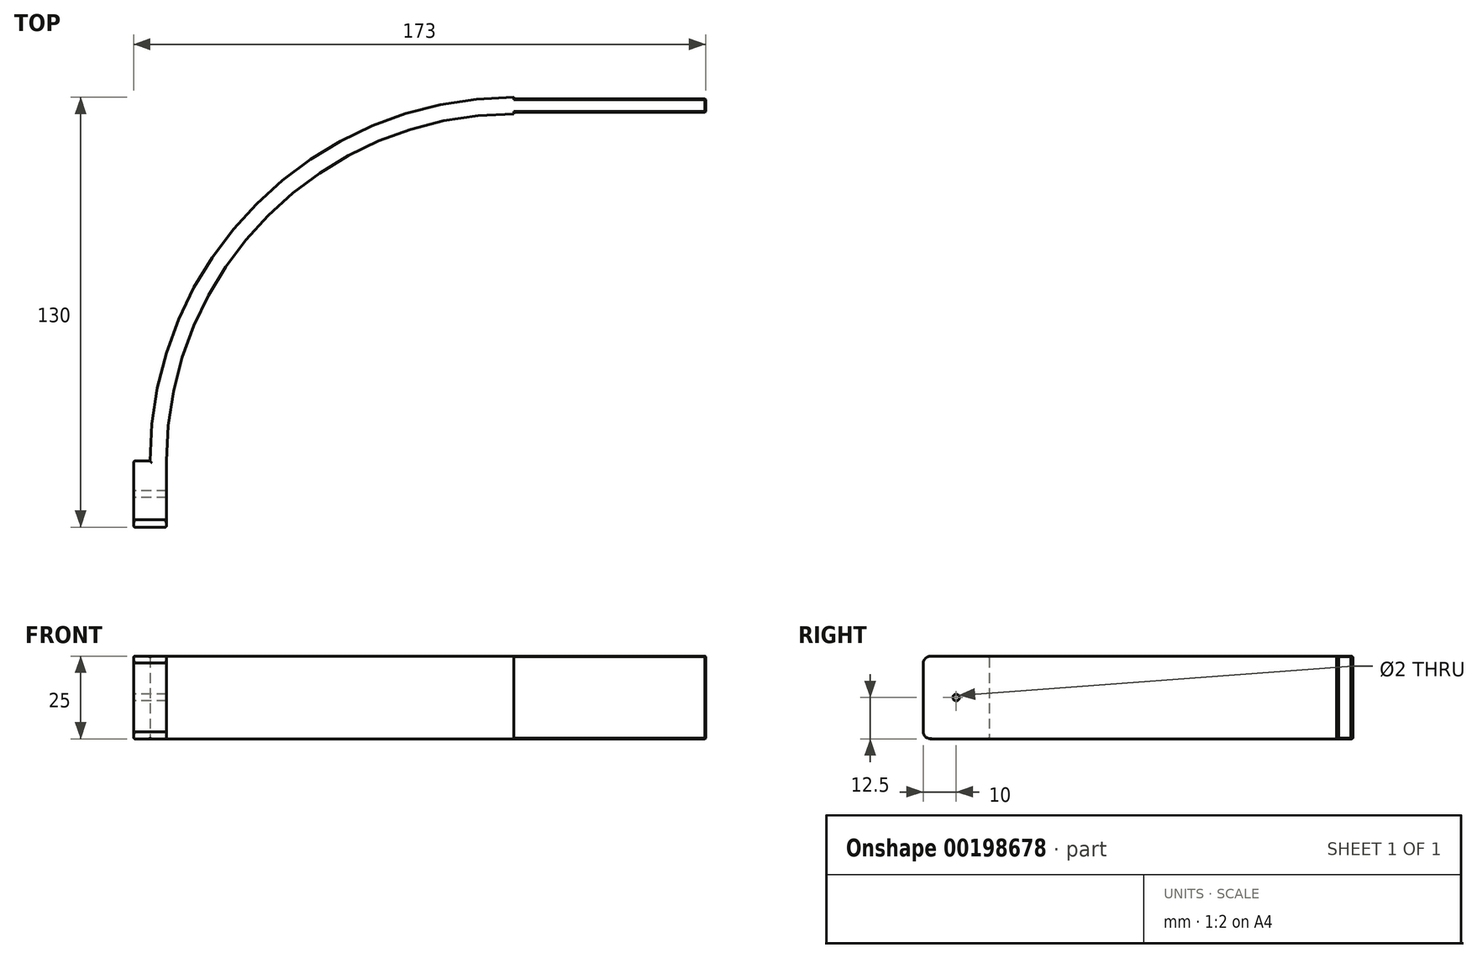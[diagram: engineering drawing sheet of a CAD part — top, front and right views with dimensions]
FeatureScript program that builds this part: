
annotation { "Feature Type Name" : "Feature", "Feature Type Description" : "" }
export const myFeature = defineFeature(function(context is Context, id is Id, definition is map)
    precondition{}
    {
        {
            var Q0;
            Q0=qCreatedBy(makeId("Top.planeOp"),FACE);
            var sketch = newSketch(context, id + "F0", { "sketchPlane" : qUnion([Q0])});
            skArc(sketch, "E0", {"start": v(-110, 0) * mm, "mid": v(-77.78, 77.78) * mm, "end": v(0, 110) * mm});
            skArc(sketch, "E1", {"start": v(-105, 0) * mm, "mid": v(-74.25, 74.25) * mm, "end": v(0, 105) * mm});
            skLineSegment(sketch, "E2", {"start": v(-105, -20) * mm, "end": v(-105, 0) * mm});
            skLineSegment(sketch, "E3", {"start": v(-110, 0) * mm, "end": v(-115, 0) * mm});
            skLineSegment(sketch, "E4", {"start": v(-115, 0) * mm, "end": v(-115, -20) * mm});
            skLineSegment(sketch, "E5", {"start": v(-115, -20) * mm, "end": v(-105, -20) * mm});
            skLineSegment(sketch, "E6", {"start": v(0, 110) * mm, "end": v(0, 109.5) * mm});
            skLineSegment(sketch, "E7", {"start": v(0, 109.5) * mm, "end": v(58, 109.5) * mm});
            skLineSegment(sketch, "E8", {"start": v(0, 105) * mm, "end": v(0, 105.5) * mm});
            skLineSegment(sketch, "E9", {"start": v(0, 105.5) * mm, "end": v(58, 105.5) * mm});
            skLineSegment(sketch, "E10", {"start": v(58, 105.5) * mm, "end": v(58, 109.5) * mm});
            skSolve(sketch);
        }
        {
            var Q0;
            Q0 = qSketchRegion(id + "F0", true);
            extrude(context, id + "F1", {"entities" : qUnion([Q0]), "depth" : 25 * mm});
        }
        {
            var Q0;
            Q0=makeQuery(id+"F1.opExtrude","SWEPT_FACE",FACE,{"disambiguationData":[OSD([sQuery(id+"F0.wireOp",EDGE,"E4")])]});
            var sketch = newSketch(context, id + "F2", { "sketchPlane" : qUnion([Q0])});
            skArc(sketch, "E11", {"start": v(17.52, 0) * mm, "mid": v(19.17, 0.55) * mm, "end": v(20, 2.09) * mm});
            skLineSegment(sketch, "E12", {"start": v(17.52, 0) * mm, "end": v(20, 0) * mm});
            skLineSegment(sketch, "E13", {"start": v(20, 0) * mm, "end": v(20, 2.09) * mm});
            skLineSegment(sketch, "E14", {"start": v(-2.5, 12.5) * mm, "end": v(22.5, 12.5) * mm, "construction": true});
            skLineSegment(sketch, "E15.MirrorCS", {"start": v(20, 25) * mm, "end": v(20, 22.91) * mm});
            skArc(sketch, "E16.MirrorCS", {"start": v(17.52, 25) * mm, "mid": v(19.17, 24.45) * mm, "end": v(20, 22.91) * mm});
            skLineSegment(sketch, "E17.MirrorCS", {"start": v(17.52, 25) * mm, "end": v(20, 25) * mm});
            skCircle(sketch, "E18", {"center": v(10, 12.5) * mm, "radius": 1 * mm});
            skSolve(sketch);
        }
        {
            var Q0;
            Q0 = qSketchRegion(id + "F2", true);
            extrude(context, id + "F3", {"entities" : qUnion([Q0]), "operationType" : NewBodyOperationType.REMOVE, "endBound" : BoundingType.THROUGH_ALL, "oppositeDirection" : true, "depth" : 25 * mm});
        }
        {
            var Q0;
            Q0=makeQuery(id+"F1.opExtrude","CAP_EDGE",EDGE,{"disambiguationData":[OSD([sQuery(id+"F0.wireOp",EDGE,"E0")])],"isStart":false});
            var Q1;
            Q1=makeQuery(id+"F1.opExtrude","CAP_EDGE",EDGE,{"disambiguationData":[OSD([sQuery(id+"F0.wireOp",EDGE,"E0")])],"isStart":true});
            var Q2;
            Q2=makeQuery(id+"F1.opExtrude","CAP_EDGE",EDGE,{"disambiguationData":[OSD([sQuery(id+"F0.wireOp",EDGE,"E4")])],"isStart":false});
            var Q3;
            Q3=makeQuery(id+"F1.opExtrude","CAP_EDGE",EDGE,{"disambiguationData":[OSD([sQuery(id+"F0.wireOp",EDGE,"E4")])],"isStart":true});
            var Q4;
            Q4=makeQuery(id+"F1.opExtrude","SWEPT_EDGE",EDGE,{"disambiguationData":[OSD([sQuery(id+"F0.wireOp",EDGE,"E3"),sQuery(id+"F0.wireOp",EDGE,"E4")])]});
            var Q5;
            Q5=makeQuery(id+"F1.opExtrude","CAP_EDGE",EDGE,{"disambiguationData":[OSD([sQuery(id+"F0.wireOp",EDGE,"E3")])],"isStart":true});
            var Q6;
            Q6=makeQuery(id+"F1.opExtrude","CAP_EDGE",EDGE,{"disambiguationData":[OSD([sQuery(id+"F0.wireOp",EDGE,"E3")])],"isStart":false});
            var Q7;
            {var subQ0=sQuery(id+"F2.wireOp",EDGE,"E11");Q7=makeQuery(id+"F3.boolean.opBoolean","COPY",EDGE,{"derivedFrom":makeQuery(id+"F3.opExtrude","CAP_EDGE",EDGE,{"disambiguationData":[OSD([subQ0]),TDD([makeQuery(id+"F2.imprint","IMPRINT",EDGE,{"disambiguationData":[TD([[makeQuery(id+"F2.imprint","INTERSECT",VERTEX,{"derivedFrom":[subQ0,sQuery(id+"F2.wireOp",EDGE,"E12")]}),-1.0]])],"derivedFrom":subQ0})])],"isStart":true})});}
            var Q8;
            Q8=makeQuery(id+"F1.opExtrude","SWEPT_EDGE",EDGE,{"disambiguationData":[OSD([sQuery(id+"F0.wireOp",EDGE,"E4"),sQuery(id+"F0.wireOp",EDGE,"E5")])]});
            var Q9;
            {var subQ0=sQuery(id+"F2.wireOp",EDGE,"E16.MirrorCS");Q9=makeQuery(id+"F3.boolean.opBoolean","COPY",EDGE,{"derivedFrom":makeQuery(id+"F3.opExtrude","CAP_EDGE",EDGE,{"disambiguationData":[OSD([subQ0]),TDD([makeQuery(id+"F2.imprint","IMPRINT",EDGE,{"disambiguationData":[TD([[makeQuery(id+"F2.imprint","INTERSECT",VERTEX,{"derivedFrom":[subQ0,sQuery(id+"F2.wireOp",EDGE,"E17.MirrorCS")]}),-1.0]])],"derivedFrom":subQ0})])],"isStart":true})});}
            fillet(context, id + "F4", {"entities" : qUnion([Q0, Q1, Q2, Q3, Q4, Q5, Q6, Q7, Q8, Q9]), "radius" : .5 * mm, "tangentPropagation" : true, "allowEdgeOverflow" : false});
        }
        {
            var Q0;
            Q0=makeQuery(id+"F1.opExtrude","SWEPT_EDGE",EDGE,{"disambiguationData":[OSD([sQuery(id+"F0.wireOp",EDGE,"E7"),sQuery(id+"F0.wireOp",EDGE,"E10")])]});
            var Q1;
            Q1=makeQuery(id+"F1.opExtrude","SWEPT_EDGE",EDGE,{"disambiguationData":[OSD([sQuery(id+"F0.wireOp",EDGE,"E9"),sQuery(id+"F0.wireOp",EDGE,"E10")])]});
            var Q2;
            Q2=makeQuery(id+"F1.opExtrude","CAP_EDGE",EDGE,{"disambiguationData":[OSD([sQuery(id+"F0.wireOp",EDGE,"E10")])],"isStart":false});
            var Q3;
            Q3=makeQuery(id+"F1.opExtrude","CAP_EDGE",EDGE,{"disambiguationData":[OSD([sQuery(id+"F0.wireOp",EDGE,"E10")])],"isStart":true});
            var Q4;
            Q4=makeQuery(id+"F1.opExtrude","CAP_EDGE",EDGE,{"disambiguationData":[OSD([sQuery(id+"F0.wireOp",EDGE,"E7")])],"isStart":false});
            var Q5;
            Q5=makeQuery(id+"F1.opExtrude","CAP_EDGE",EDGE,{"disambiguationData":[OSD([sQuery(id+"F0.wireOp",EDGE,"E7")])],"isStart":true});
            var Q6;
            Q6=makeQuery(id+"F1.opExtrude","CAP_EDGE",EDGE,{"disambiguationData":[OSD([sQuery(id+"F0.wireOp",EDGE,"E9")])],"isStart":true});
            var Q7;
            Q7=makeQuery(id+"F1.opExtrude","CAP_EDGE",EDGE,{"disambiguationData":[OSD([sQuery(id+"F0.wireOp",EDGE,"E9")])],"isStart":false});
            chamfer(context, id + "F5", {"entities" : qUnion([Q0, Q1, Q2, Q3, Q4, Q5, Q6, Q7]), "width" : .2 * mm, "tangentPropagation" : true});
        }
        {
            var Q0;
            Q0=makeQuery(id+"F1.opExtrude","CAP_EDGE",EDGE,{"disambiguationData":[OSD([sQuery(id+"F0.wireOp",EDGE,"E1")])],"isStart":false});
            var Q1;
            Q1=makeQuery(id+"F1.opExtrude","CAP_EDGE",EDGE,{"disambiguationData":[OSD([sQuery(id+"F0.wireOp",EDGE,"E1")])],"isStart":true});
            var Q2;
            {var subQ0=sQuery(id+"F2.wireOp",EDGE,"E16.MirrorCS");Q2=makeQuery(id+"F3.boolean.opBoolean","INTERSECT",EDGE,{"derivedFrom":[makeQuery(id+"F1.opExtrude","SWEPT_FACE",FACE,{"disambiguationData":[OSD([sQuery(id+"F0.wireOp",EDGE,"E2")])]}),makeQuery(id+"F3.opExtrude","SWEPT_FACE",FACE,{"disambiguationData":[OSD([subQ0]),TDD([makeQuery(id+"F2.imprint","IMPRINT",EDGE,{"disambiguationData":[TD([[makeQuery(id+"F2.imprint","INTERSECT",VERTEX,{"derivedFrom":[subQ0,sQuery(id+"F2.wireOp",EDGE,"E17.MirrorCS")]}),-1.0]])],"derivedFrom":subQ0})])]})]});}
            var Q3;
            Q3=makeQuery(id+"F1.opExtrude","SWEPT_EDGE",EDGE,{"disambiguationData":[OSD([sQuery(id+"F0.wireOp",EDGE,"E2"),sQuery(id+"F0.wireOp",EDGE,"E5")])]});
            var Q4;
            {var subQ0=sQuery(id+"F2.wireOp",EDGE,"E11");Q4=makeQuery(id+"F3.boolean.opBoolean","INTERSECT",EDGE,{"derivedFrom":[makeQuery(id+"F1.opExtrude","SWEPT_FACE",FACE,{"disambiguationData":[OSD([sQuery(id+"F0.wireOp",EDGE,"E2")])]}),makeQuery(id+"F3.opExtrude","SWEPT_FACE",FACE,{"disambiguationData":[OSD([subQ0]),TDD([makeQuery(id+"F2.imprint","IMPRINT",EDGE,{"disambiguationData":[TD([[makeQuery(id+"F2.imprint","INTERSECT",VERTEX,{"derivedFrom":[subQ0,sQuery(id+"F2.wireOp",EDGE,"E12")]}),-1.0]])],"derivedFrom":subQ0})])]})]});}
            var Q5;
            Q5=makeQuery(id+"F1.opExtrude","CAP_EDGE",EDGE,{"disambiguationData":[OSD([sQuery(id+"F0.wireOp",EDGE,"E2")])],"isStart":true});
            var Q6;
            Q6=makeQuery(id+"F1.opExtrude","CAP_EDGE",EDGE,{"disambiguationData":[OSD([sQuery(id+"F0.wireOp",EDGE,"E2")])],"isStart":false});
            fillet(context, id + "F6", {"entities" : qUnion([Q0, Q1, Q2, Q3, Q4, Q5, Q6]), "radius" : .5 * mm, "tangentPropagation" : true, "allowEdgeOverflow" : false});
        }
    });
